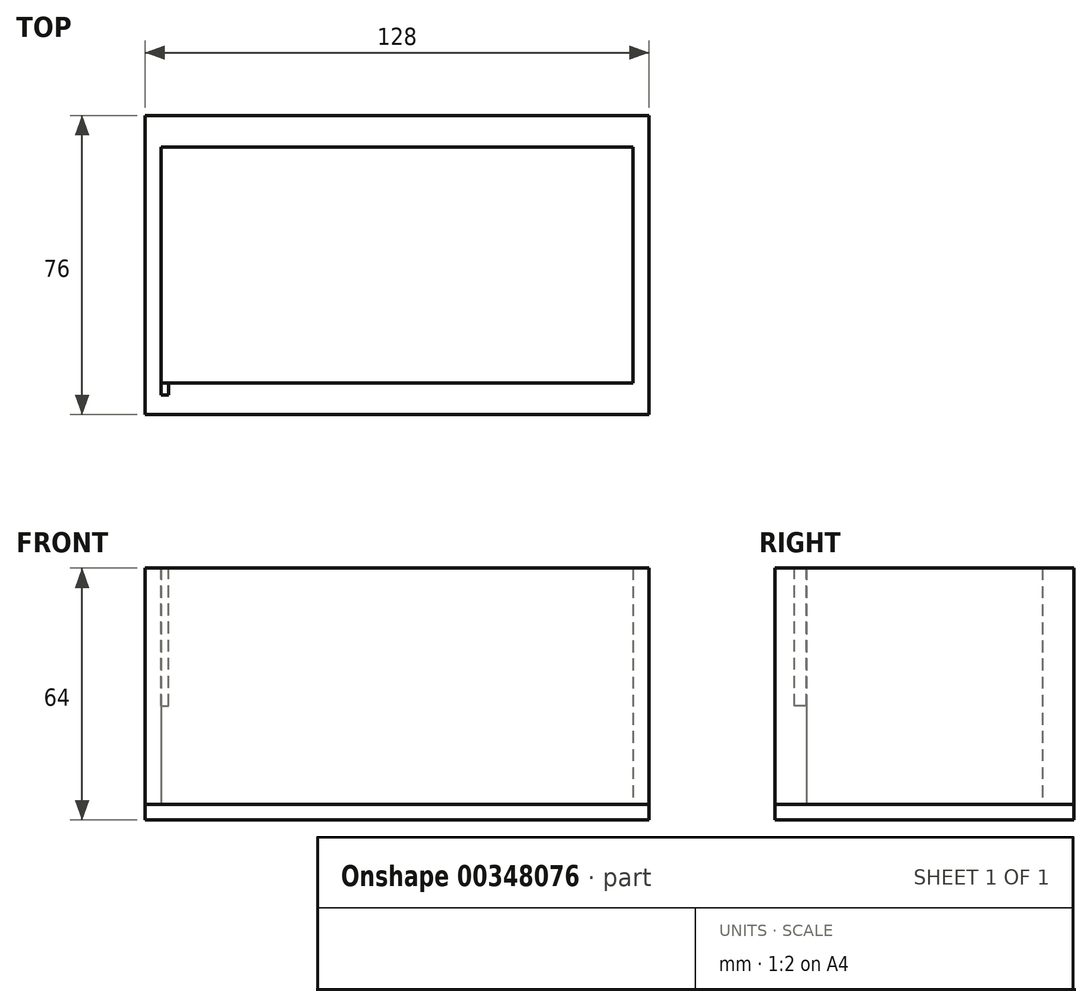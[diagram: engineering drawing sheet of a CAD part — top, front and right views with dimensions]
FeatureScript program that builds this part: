
annotation { "Feature Type Name" : "Feature", "Feature Type Description" : "" }
export const myFeature = defineFeature(function(context is Context, id is Id, definition is map)
    precondition{}
    {
        {
            var Q0;
            Q0=qCreatedBy(makeId("Top.planeOp"),FACE);
            var sketch = newSketch(context, id + "F0", { "sketchPlane" : qUnion([Q0])});
            skLineSegment(sketch, "E0.bottom", {"start": v(-60, 30) * mm, "end": v(60, 30) * mm});
            skLineSegment(sketch, "E0.top", {"start": v(-60, -30) * mm, "end": v(60, -30) * mm});
            skLineSegment(sketch, "E0.left", {"start": v(-60, 30) * mm, "end": v(-60, -30) * mm});
            skLineSegment(sketch, "E0.right", {"start": v(60, 30) * mm, "end": v(60, -30) * mm});
            skPoint(sketch, "E0.middle", {"position": v(0, 0) * mm});
            skLineSegment(sketch, "E1.0", {"start": v(-64, 38) * mm, "end": v(-64, -38) * mm});
            skLineSegment(sketch, "E1.1", {"start": v(-64, 38) * mm, "end": v(64, 38) * mm});
            skLineSegment(sketch, "E1.2", {"start": v(64, 38) * mm, "end": v(64, -38) * mm});
            skLineSegment(sketch, "E1.3", {"start": v(-64, -38) * mm, "end": v(64, -38) * mm});
            skSolve(sketch);
        }
        {
            var Q0;
            Q0=makeQuery(id+"F0.imprint","IMPRINT",FACE,{"disambiguationData":[TD([[makeQuery(id+"F0.imprint","IMPRINT",EDGE,{"derivedFrom":sQuery(id+"F0.wireOp",EDGE,"E0.bottom")}),1.0]])]});
            extrude(context, id + "F1", {"entities" : qUnion([Q0]), "depth" : 60 * mm});
        }
        {
            var Q0;
            Q0=makeQuery(id+"F1.opExtrude","CAP_FACE",FACE,{"disambiguationData":[OSD([sQuery(id+"F0.wireOp",EDGE,"E0.bottom"),sQuery(id+"F0.wireOp",EDGE,"E0.top"),sQuery(id+"F0.wireOp",EDGE,"E0.left"),sQuery(id+"F0.wireOp",EDGE,"E0.right"),sQuery(id+"F0.wireOp",EDGE,"E1.0"),sQuery(id+"F0.wireOp",EDGE,"E1.1"),sQuery(id+"F0.wireOp",EDGE,"E1.2"),sQuery(id+"F0.wireOp",EDGE,"E1.3")])],"isStart":false});
            var sketch = newSketch(context, id + "F2", { "sketchPlane" : qUnion([Q0])});
            skLineSegment(sketch, "E2.bottom", {"start": v(-60, -30) * mm, "end": v(-58, -30) * mm});
            skLineSegment(sketch, "E2.top", {"start": v(-60, -33) * mm, "end": v(-58, -33) * mm});
            skLineSegment(sketch, "E2.left", {"start": v(-60, -30) * mm, "end": v(-60, -33) * mm});
            skLineSegment(sketch, "E2.right", {"start": v(-58, -30) * mm, "end": v(-58, -33) * mm});
            skSolve(sketch);
        }
        {
            var Q0;
            Q0=makeQuery(id+"F2.imprint","IMPRINT",FACE,{"disambiguationData":[TD([[makeQuery(id+"F2.imprint","IMPRINT",EDGE,{"derivedFrom":sQuery(id+"F2.wireOp",EDGE,"E2.bottom")}),-1.0]])]});
            extrude(context, id + "F3", {"entities" : qUnion([Q0]), "operationType" : NewBodyOperationType.REMOVE, "oppositeDirection" : true, "depth" : 35 * mm});
        }
        {
            var Q0;
            Q0=makeQuery(id+"F1.opExtrude","CAP_FACE",FACE,{"disambiguationData":[OSD([sQuery(id+"F0.wireOp",EDGE,"E0.bottom"),sQuery(id+"F0.wireOp",EDGE,"E0.top"),sQuery(id+"F0.wireOp",EDGE,"E0.left"),sQuery(id+"F0.wireOp",EDGE,"E0.right"),sQuery(id+"F0.wireOp",EDGE,"E1.0"),sQuery(id+"F0.wireOp",EDGE,"E1.1"),sQuery(id+"F0.wireOp",EDGE,"E1.2"),sQuery(id+"F0.wireOp",EDGE,"E1.3")])],"isStart":true});
            var sketch = newSketch(context, id + "F4", { "sketchPlane" : qUnion([Q0])});
            skLineSegment(sketch, "E3.bottom", {"start": v(-64, 38) * mm, "end": v(64, 38) * mm});
            skLineSegment(sketch, "E3.top", {"start": v(-64, -38) * mm, "end": v(64, -38) * mm});
            skLineSegment(sketch, "E3.left", {"start": v(-64, 38) * mm, "end": v(-64, -38) * mm});
            skLineSegment(sketch, "E3.right", {"start": v(64, 38) * mm, "end": v(64, -38) * mm});
            skPoint(sketch, "E3.middle", {"position": v(0, 0) * mm});
            skSolve(sketch);
        }
        {
            var Q0;
            Q0 = qSketchRegion(id + "F4", true);
            extrude(context, id + "F5", {"entities" : qUnion([Q0]), "depth" : 4 * mm});
        }
    });
